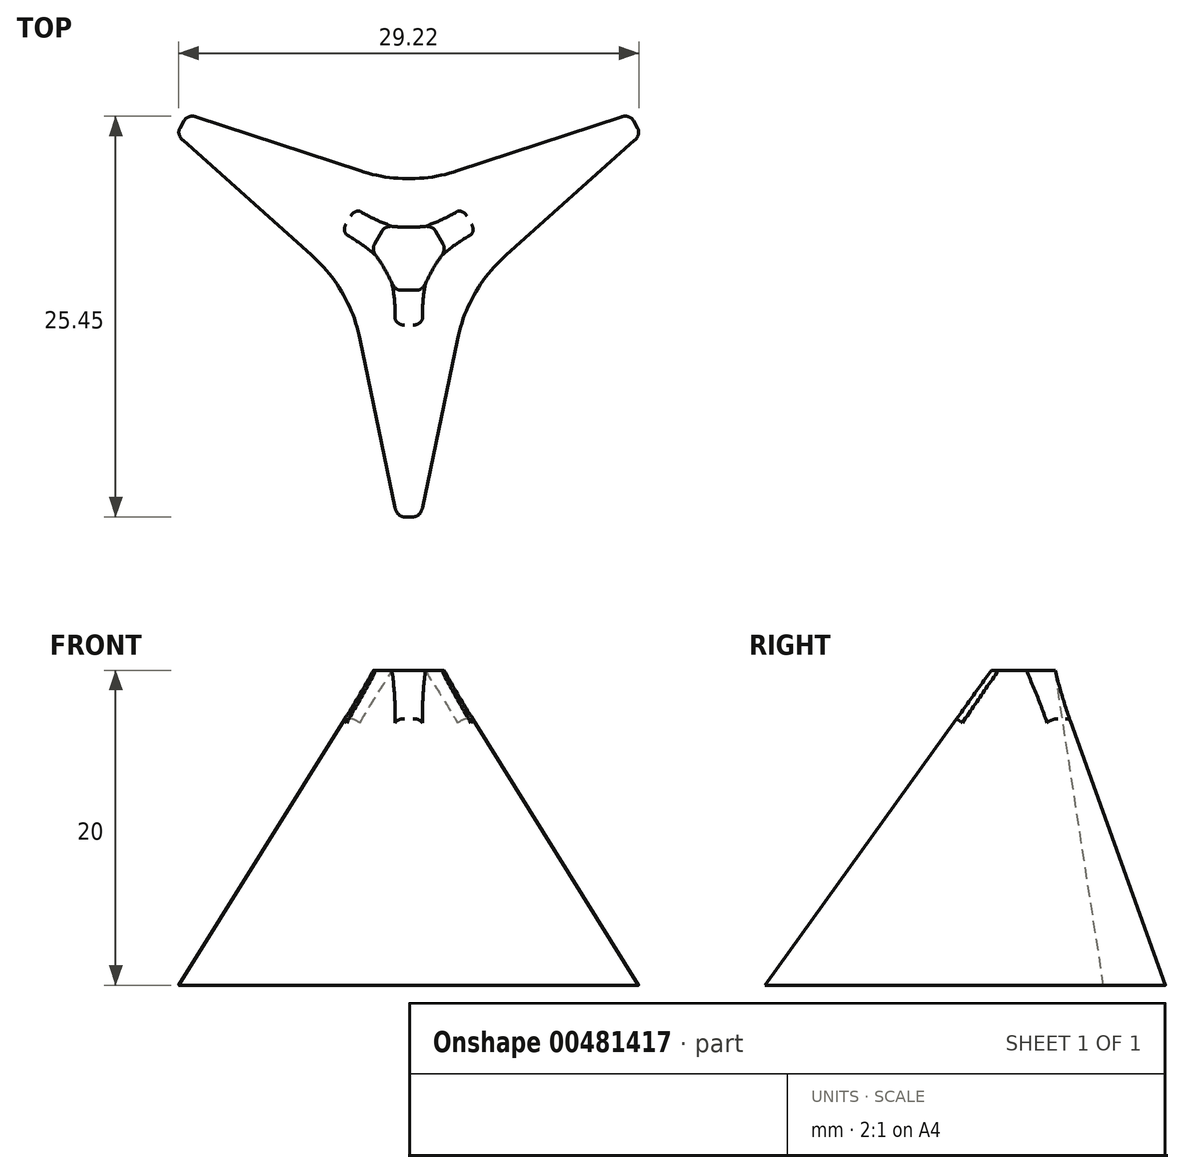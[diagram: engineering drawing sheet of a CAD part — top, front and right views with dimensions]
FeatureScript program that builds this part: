
annotation { "Feature Type Name" : "Feature", "Feature Type Description" : "" }
export const myFeature = defineFeature(function(context is Context, id is Id, definition is map)
    precondition{}
    {
        {
            var Q0;
            Q0=qCreatedBy(makeId("Top.planeOp"),FACE);
            var sketch = newSketch(context, id + "F0", { "sketchPlane" : qUnion([Q0])});
            skCircle(sketch, "E0.cCircle", {"center": v(0, 0) * mm, "radius": 10.1 * mm, "construction": true});
            skLineSegment(sketch, "E0.0", {"start": v(17.5, 10.1) * mm, "end": v(0, -20.2) * mm, "construction": true});
            skLineSegment(sketch, "E0.1", {"start": v(0, -20.2) * mm, "end": v(-17.5, 10.1) * mm, "construction": true});
            skLineSegment(sketch, "E0.2", {"start": v(-17.5, 10.1) * mm, "end": v(17.5, 10.1) * mm, "construction": true});
            skPoint(sketch, "E0.0.midPoint", {"position": v(8.75, -5.05) * mm});
            skCircle(sketch, "E1.cCircle", {"center": v(0, 0) * mm, "radius": 4.33 * mm, "construction": true});
            skLineSegment(sketch, "E1.0", {"start": v(7.5, 4.33) * mm, "end": v(0, -8.66) * mm, "construction": true});
            skLineSegment(sketch, "E1.1", {"start": v(0, -8.66) * mm, "end": v(-7.5, 4.33) * mm, "construction": true});
            skLineSegment(sketch, "E1.2", {"start": v(-7.5, 4.33) * mm, "end": v(7.5, 4.33) * mm, "construction": true});
            skPoint(sketch, "E1.0.midPoint", {"position": v(2.48, 0) * mm});
            skPoint(sketch, "E2", {"position": v(0, 4.33) * mm});
            skPoint(sketch, "E3", {"position": v(3.75, -2.17) * mm});
            skPoint(sketch, "E4", {"position": v(-3.75, -2.17) * mm});
            skLineSegment(sketch, "E5", {"start": v(-17.5, 10.1) * mm, "end": v(0, 4.33) * mm});
            skLineSegment(sketch, "E6", {"start": v(0, 4.33) * mm, "end": v(17.5, 10.1) * mm});
            skLineSegment(sketch, "E7", {"start": v(17.5, 10.1) * mm, "end": v(3.75, -2.17) * mm});
            skLineSegment(sketch, "E8", {"start": v(3.75, -2.17) * mm, "end": v(0, -20.2) * mm});
            skLineSegment(sketch, "E9", {"start": v(0, -20.2) * mm, "end": v(-3.75, -2.17) * mm});
            skLineSegment(sketch, "E10", {"start": v(-3.75, -2.17) * mm, "end": v(-17.5, 10.1) * mm});
            skSolve(sketch);
        }
        {
            var Q0;
            Q0=qCreatedBy(makeId("Top.planeOp"),FACE);
            cPlane(context, id + "F1", {"entities" : qUnion([Q0]), "cplaneType" : CPlaneType.OFFSET, "offset" : 20 * mm, "width" : 150 * mm, "height" : 150 * mm});
        }
        {
            var Q0;
            Q0=qCreatedBy(id+"F1.planeOp",FACE);
            var sketch = newSketch(context, id + "F2", { "sketchPlane" : qUnion([Q0])});
            skLineSegment(sketch, "E11", {"start": v(-5.03, 2.9) * mm, "end": v(0, 1.25) * mm});
            skLineSegment(sketch, "E12", {"start": v(0, 1.25) * mm, "end": v(5.03, 2.9) * mm});
            skLineSegment(sketch, "E13", {"start": v(5.03, 2.9) * mm, "end": v(1.08, -0.62) * mm});
            skLineSegment(sketch, "E14", {"start": v(1.08, -0.62) * mm, "end": v(0, -5.81) * mm});
            skLineSegment(sketch, "E15", {"start": v(0, -5.81) * mm, "end": v(-1.08, -0.62) * mm});
            skLineSegment(sketch, "E16", {"start": v(-1.08, -0.62) * mm, "end": v(-5.03, 2.9) * mm});
            skLineSegment(sketch, "E17", {"start": v(1.08, -0.62) * mm, "end": v(0, 0) * mm, "construction": true});
            skLineSegment(sketch, "E18", {"start": v(0, 0) * mm, "end": v(-1.08, -0.62) * mm, "construction": true});
            skLineSegment(sketch, "E19", {"start": v(0, 1.25) * mm, "end": v(0, 0) * mm, "construction": true});
            skSolve(sketch);
        }
        {
            var Q0;
            Q0=makeQuery(id+"F0.imprint","IMPRINT",FACE,{"disambiguationData":[TD([[makeQuery(id+"F0.imprint","IMPRINT",EDGE,{"derivedFrom":sQuery(id+"F0.wireOp",EDGE,"E5")}),-1.0]])]});
            var Q1;
            Q1=makeQuery(id+"F2.imprint","IMPRINT",FACE,{"disambiguationData":[TD([[makeQuery(id+"F2.imprint","IMPRINT",EDGE,{"derivedFrom":sQuery(id+"F2.wireOp",EDGE,"E11")}),-1.0]])]});
            loft(context, id + "F3", {"sheetProfilesArray" : [{ "sheetProfileEntities" : qUnion([Q0]) }, { "sheetProfileEntities" : qUnion([Q1]) }]});
        }
        {
            var Q0;
            Q0=makeQuery(id+"F3.opLoft","SWEPT_EDGE",EDGE,{"disambiguationData":[OSD([sQuery(id+"F0.wireOp",EDGE,"E7"),sQuery(id+"F0.wireOp",EDGE,"E8"),sQuery(id+"F2.wireOp",EDGE,"E13"),sQuery(id+"F2.wireOp",EDGE,"E14")])]});
            var Q1;
            Q1=makeQuery(id+"F3.opLoft","SWEPT_EDGE",EDGE,{"disambiguationData":[OSD([sQuery(id+"F0.wireOp",EDGE,"E9"),sQuery(id+"F0.wireOp",EDGE,"E10"),sQuery(id+"F2.wireOp",EDGE,"E15"),sQuery(id+"F2.wireOp",EDGE,"E16")])]});
            var Q2;
            Q2=makeQuery(id+"F3.opLoft","SWEPT_EDGE",EDGE,{"disambiguationData":[OSD([sQuery(id+"F0.wireOp",EDGE,"E5"),sQuery(id+"F0.wireOp",EDGE,"E6"),sQuery(id+"F2.wireOp",EDGE,"E11"),sQuery(id+"F2.wireOp",EDGE,"E12")])]});
            fillet(context, id + "F4", {"entities" : qUnion([Q0, Q1, Q2]), "radius" : 10 * mm, "tangentPropagation" : true, "allowEdgeOverflow" : false});
        }
        {
            var Q0;
            Q0=makeQuery(id+"F3.opLoft","SWEPT_EDGE",EDGE,{"disambiguationData":[OSD([sQuery(id+"F0.wireOp",EDGE,"E8"),sQuery(id+"F0.wireOp",EDGE,"E9"),sQuery(id+"F2.wireOp",EDGE,"E14"),sQuery(id+"F2.wireOp",EDGE,"E15")])]});
            var Q1;
            Q1=makeQuery(id+"F3.opLoft","SWEPT_EDGE",EDGE,{"disambiguationData":[OSD([sQuery(id+"F0.wireOp",EDGE,"E6"),sQuery(id+"F0.wireOp",EDGE,"E7"),sQuery(id+"F2.wireOp",EDGE,"E12"),sQuery(id+"F2.wireOp",EDGE,"E13")])]});
            var Q2;
            Q2=makeQuery(id+"F3.opLoft","SWEPT_EDGE",EDGE,{"disambiguationData":[OSD([sQuery(id+"F0.wireOp",EDGE,"E5"),sQuery(id+"F0.wireOp",EDGE,"E10"),sQuery(id+"F2.wireOp",EDGE,"E11"),sQuery(id+"F2.wireOp",EDGE,"E16")])]});
            chamfer(context, id + "F5", {"entities" : qUnion([Q0, Q1, Q2]), "width" : 3 * mm, "tangentPropagation" : true});
        }
        {
            var Q0;
            {var subQ0=sQuery(id+"F2.wireOp",EDGE,"E16");var subQ1=sQuery(id+"F2.wireOp",EDGE,"E11");var subQ2=sQuery(id+"F0.wireOp",EDGE,"E10");var subQ3=sQuery(id+"F0.wireOp",EDGE,"E5");Q0=makeQuery(id+"F5.opChamfer","BLEND_EDGE",EDGE,{"blendedFrom":[makeQuery(id+"F3.opLoft","SWEPT_EDGE",EDGE,{"disambiguationData":[OSD([subQ3,subQ2,subQ1,subQ0])]}),makeQuery(id+"F3.opLoft","SWEPT_FACE",FACE,{"disambiguationData":[OSD([subQ3,sQuery(id+"F0.wireOp",EDGE,"E9"),subQ2,subQ1,sQuery(id+"F2.wireOp",EDGE,"E15"),subQ0])]})],"blendedInto":[makeQuery(id+"F3.opLoft","SWEPT_FACE",FACE,{"disambiguationData":[OSD([subQ3,sQuery(id+"F0.wireOp",EDGE,"E9"),subQ2,subQ1,sQuery(id+"F2.wireOp",EDGE,"E15"),subQ0])]})]});}
            var Q1;
            {var subQ0=sQuery(id+"F2.wireOp",EDGE,"E16");var subQ1=sQuery(id+"F2.wireOp",EDGE,"E11");var subQ2=sQuery(id+"F0.wireOp",EDGE,"E10");var subQ3=sQuery(id+"F0.wireOp",EDGE,"E5");Q1=makeQuery(id+"F5.opChamfer","BLEND_EDGE",EDGE,{"blendedFrom":[makeQuery(id+"F3.opLoft","SWEPT_EDGE",EDGE,{"disambiguationData":[OSD([subQ3,subQ2,subQ1,subQ0])]}),makeQuery(id+"F3.opLoft","SWEPT_FACE",FACE,{"disambiguationData":[OSD([subQ3,sQuery(id+"F0.wireOp",EDGE,"E6"),subQ2,subQ1,sQuery(id+"F2.wireOp",EDGE,"E12"),subQ0])]})],"blendedInto":[makeQuery(id+"F3.opLoft","SWEPT_FACE",FACE,{"disambiguationData":[OSD([subQ3,sQuery(id+"F0.wireOp",EDGE,"E6"),subQ2,subQ1,sQuery(id+"F2.wireOp",EDGE,"E12"),subQ0])]})]});}
            var Q2;
            {var subQ0=sQuery(id+"F2.wireOp",EDGE,"E13");var subQ1=sQuery(id+"F2.wireOp",EDGE,"E12");var subQ2=sQuery(id+"F0.wireOp",EDGE,"E7");var subQ3=sQuery(id+"F0.wireOp",EDGE,"E6");Q2=makeQuery(id+"F5.opChamfer","BLEND_EDGE",EDGE,{"blendedFrom":[makeQuery(id+"F3.opLoft","SWEPT_EDGE",EDGE,{"disambiguationData":[OSD([subQ3,subQ2,subQ1,subQ0])]}),makeQuery(id+"F3.opLoft","SWEPT_FACE",FACE,{"disambiguationData":[OSD([sQuery(id+"F0.wireOp",EDGE,"E5"),subQ3,subQ2,sQuery(id+"F2.wireOp",EDGE,"E11"),subQ1,subQ0])]})],"blendedInto":[makeQuery(id+"F3.opLoft","SWEPT_FACE",FACE,{"disambiguationData":[OSD([sQuery(id+"F0.wireOp",EDGE,"E5"),subQ3,subQ2,sQuery(id+"F2.wireOp",EDGE,"E11"),subQ1,subQ0])]})]});}
            var Q3;
            {var subQ0=sQuery(id+"F2.wireOp",EDGE,"E13");var subQ1=sQuery(id+"F2.wireOp",EDGE,"E12");var subQ2=sQuery(id+"F0.wireOp",EDGE,"E7");var subQ3=sQuery(id+"F0.wireOp",EDGE,"E6");Q3=makeQuery(id+"F5.opChamfer","BLEND_EDGE",EDGE,{"blendedFrom":[makeQuery(id+"F3.opLoft","SWEPT_EDGE",EDGE,{"disambiguationData":[OSD([subQ3,subQ2,subQ1,subQ0])]}),makeQuery(id+"F3.opLoft","SWEPT_FACE",FACE,{"disambiguationData":[OSD([subQ3,subQ2,sQuery(id+"F0.wireOp",EDGE,"E8"),subQ1,subQ0,sQuery(id+"F2.wireOp",EDGE,"E14")])]})],"blendedInto":[makeQuery(id+"F3.opLoft","SWEPT_FACE",FACE,{"disambiguationData":[OSD([subQ3,subQ2,sQuery(id+"F0.wireOp",EDGE,"E8"),subQ1,subQ0,sQuery(id+"F2.wireOp",EDGE,"E14")])]})]});}
            var Q4;
            {var subQ0=sQuery(id+"F2.wireOp",EDGE,"E15");var subQ1=sQuery(id+"F2.wireOp",EDGE,"E14");var subQ2=sQuery(id+"F0.wireOp",EDGE,"E9");var subQ3=sQuery(id+"F0.wireOp",EDGE,"E8");Q4=makeQuery(id+"F5.opChamfer","BLEND_EDGE",EDGE,{"blendedFrom":[makeQuery(id+"F3.opLoft","SWEPT_EDGE",EDGE,{"disambiguationData":[OSD([subQ3,subQ2,subQ1,subQ0])]}),makeQuery(id+"F3.opLoft","SWEPT_FACE",FACE,{"disambiguationData":[OSD([sQuery(id+"F0.wireOp",EDGE,"E7"),subQ3,subQ2,sQuery(id+"F2.wireOp",EDGE,"E13"),subQ1,subQ0])]})],"blendedInto":[makeQuery(id+"F3.opLoft","SWEPT_FACE",FACE,{"disambiguationData":[OSD([sQuery(id+"F0.wireOp",EDGE,"E7"),subQ3,subQ2,sQuery(id+"F2.wireOp",EDGE,"E13"),subQ1,subQ0])]})]});}
            var Q5;
            {var subQ0=sQuery(id+"F2.wireOp",EDGE,"E15");var subQ1=sQuery(id+"F2.wireOp",EDGE,"E14");var subQ2=sQuery(id+"F0.wireOp",EDGE,"E9");var subQ3=sQuery(id+"F0.wireOp",EDGE,"E8");Q5=makeQuery(id+"F5.opChamfer","BLEND_EDGE",EDGE,{"blendedFrom":[makeQuery(id+"F3.opLoft","SWEPT_EDGE",EDGE,{"disambiguationData":[OSD([subQ3,subQ2,subQ1,subQ0])]}),makeQuery(id+"F3.opLoft","SWEPT_FACE",FACE,{"disambiguationData":[OSD([subQ3,subQ2,sQuery(id+"F0.wireOp",EDGE,"E10"),subQ1,subQ0,sQuery(id+"F2.wireOp",EDGE,"E16")])]})],"blendedInto":[makeQuery(id+"F3.opLoft","SWEPT_FACE",FACE,{"disambiguationData":[OSD([subQ3,subQ2,sQuery(id+"F0.wireOp",EDGE,"E10"),subQ1,subQ0,sQuery(id+"F2.wireOp",EDGE,"E16")])]})]});}
            fillet(context, id + "F6", {"entities" : qUnion([Q0, Q1, Q2, Q3, Q4, Q5]), "radius" : 0.6 * mm, "tangentPropagation" : true, "allowEdgeOverflow" : false});
        }
    });
